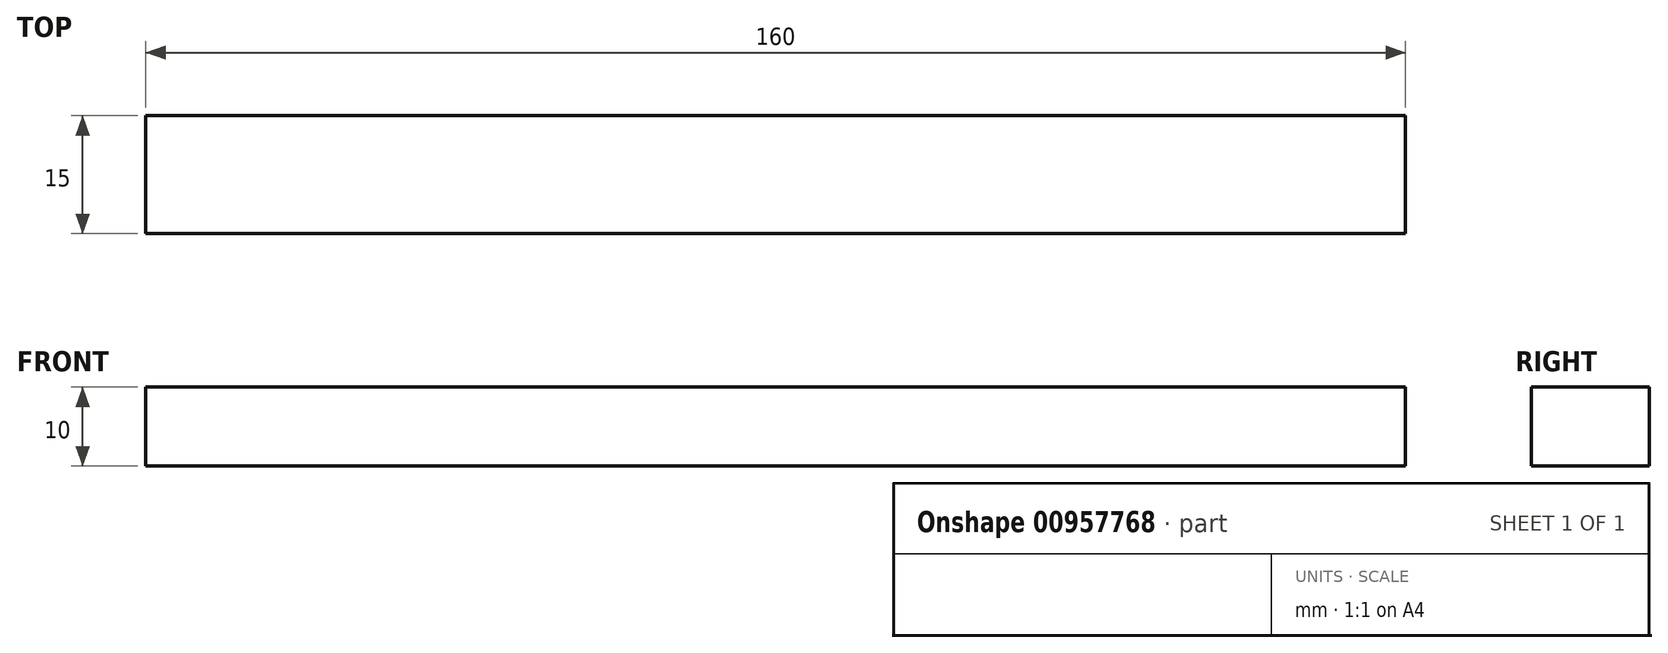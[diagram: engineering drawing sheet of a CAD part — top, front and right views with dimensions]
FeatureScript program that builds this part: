
annotation { "Feature Type Name" : "Feature", "Feature Type Description" : "" }
export const myFeature = defineFeature(function(context is Context, id is Id, definition is map)
    precondition{}
    {
        {
            var Q0;
            Q0=qCreatedBy(makeId("Top.planeOp"),FACE);
            var sketch = newSketch(context, id + "F0", { "sketchPlane" : qUnion([Q0])});
            skLineSegment(sketch, "E0.bottom", {"start": v(-80, 7.5) * mm, "end": v(80, 7.5) * mm});
            skLineSegment(sketch, "E0.top", {"start": v(-80, -7.5) * mm, "end": v(80, -7.5) * mm});
            skLineSegment(sketch, "E0.left", {"start": v(-80, 7.5) * mm, "end": v(-80, -7.5) * mm});
            skLineSegment(sketch, "E0.right", {"start": v(80, 7.5) * mm, "end": v(80, -7.5) * mm});
            skPoint(sketch, "E0.middle", {"position": v(0, 0) * mm});
            skLineSegment(sketch, "E1.bottom", {"start": v(-80, 7.5) * mm, "end": v(-92.2, 7.5) * mm});
            skLineSegment(sketch, "E1.top", {"start": v(-80, -7.5) * mm, "end": v(-92.2, -7.5) * mm});
            skLineSegment(sketch, "E1.right", {"start": v(-92.2, 7.5) * mm, "end": v(-92.2, -7.5) * mm});
            skSolve(sketch);
        }
        {
            var Q0;
            Q0=makeQuery(id+"F0.imprint","IMPRINT",FACE,{"disambiguationData":[TD([[makeQuery(id+"F0.imprint","IMPRINT",EDGE,{"derivedFrom":sQuery(id+"F0.wireOp",EDGE,"E0.bottom")}),-1.0]])]});
            extrude(context, id + "F1", {"entities" : qUnion([Q0]), "depth" : 10 * mm, "offsetDistance" : 25 * mm});
        }
    });
